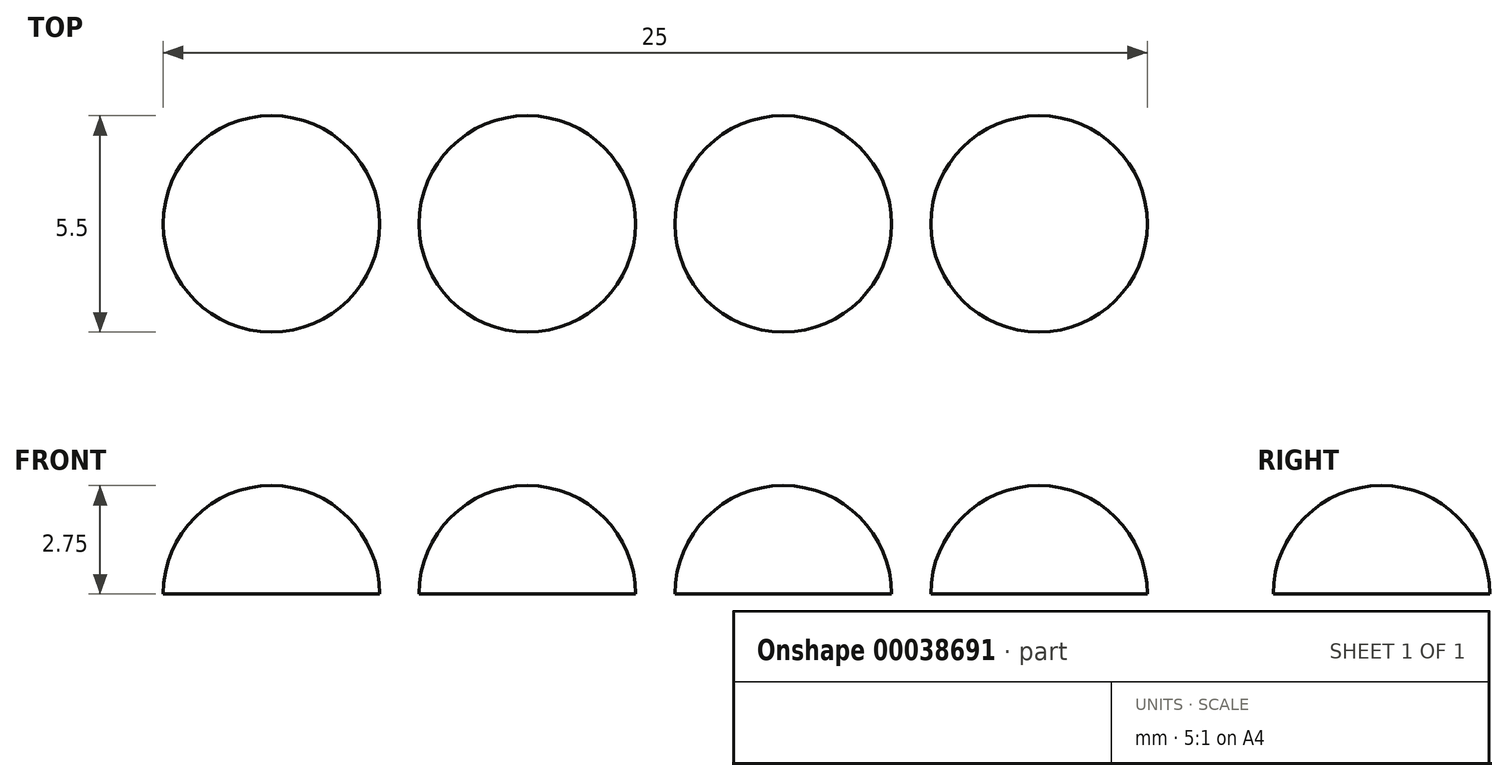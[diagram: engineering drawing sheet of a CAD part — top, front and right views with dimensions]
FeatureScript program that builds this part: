
annotation { "Feature Type Name" : "Feature", "Feature Type Description" : "" }
export const myFeature = defineFeature(function(context is Context, id is Id, definition is map)
    precondition{}
    {
        {
            var Q0;
            Q0=qCreatedBy(makeId("Top.planeOp"),FACE);
            var sketch = newSketch(context, id + "F0", { "sketchPlane" : qUnion([Q0])});
            skLineSegment(sketch, "E0", {"start": v(-2.75, 0) * mm, "end": v(2.75, 0) * mm});
            skArc(sketch, "E1", {"start": v(2.75, 0) * mm, "mid": v(0, 2.75) * mm, "end": v(-2.75, 0) * mm});
            skLineSegment(sketch, "E2.1.0.0", {"start": v(3.75, 0) * mm, "end": v(9.25, 0) * mm});
            skArc(sketch, "E2.1.0.1", {"start": v(9.25, 0) * mm, "mid": v(6.5, 2.75) * mm, "end": v(3.75, 0) * mm});
            skLineSegment(sketch, "E2.2.0.0", {"start": v(10.25, 0) * mm, "end": v(15.75, 0) * mm});
            skArc(sketch, "E2.2.0.1", {"start": v(15.75, 0) * mm, "mid": v(13, 2.75) * mm, "end": v(10.25, 0) * mm});
            skLineSegment(sketch, "E2.3.0.0", {"start": v(16.75, 0) * mm, "end": v(22.25, 0) * mm});
            skArc(sketch, "E2.3.0.1", {"start": v(22.25, 0) * mm, "mid": v(19.5, 2.75) * mm, "end": v(16.75, 0) * mm});
            skLineSegment(sketch, "E2.direction1", {"start": v(-2.75, 0) * mm, "end": v(3.75, 0) * mm, "construction": true});
            skSolve(sketch);
        }
        {
            var Q0;
            Q0 = qSketchRegion(id + "F0", true);
            var Q1;
            Q1=sQuery(id+"F0.wireOp",EDGE,"E0");
            revolve(context, id + "F1", {"entities" : qUnion([Q0]), "axis" : qUnion([Q1]), "revolveType" : RevolveType.ONE_DIRECTION, "angle" : 180 * degree});
        }
    });
